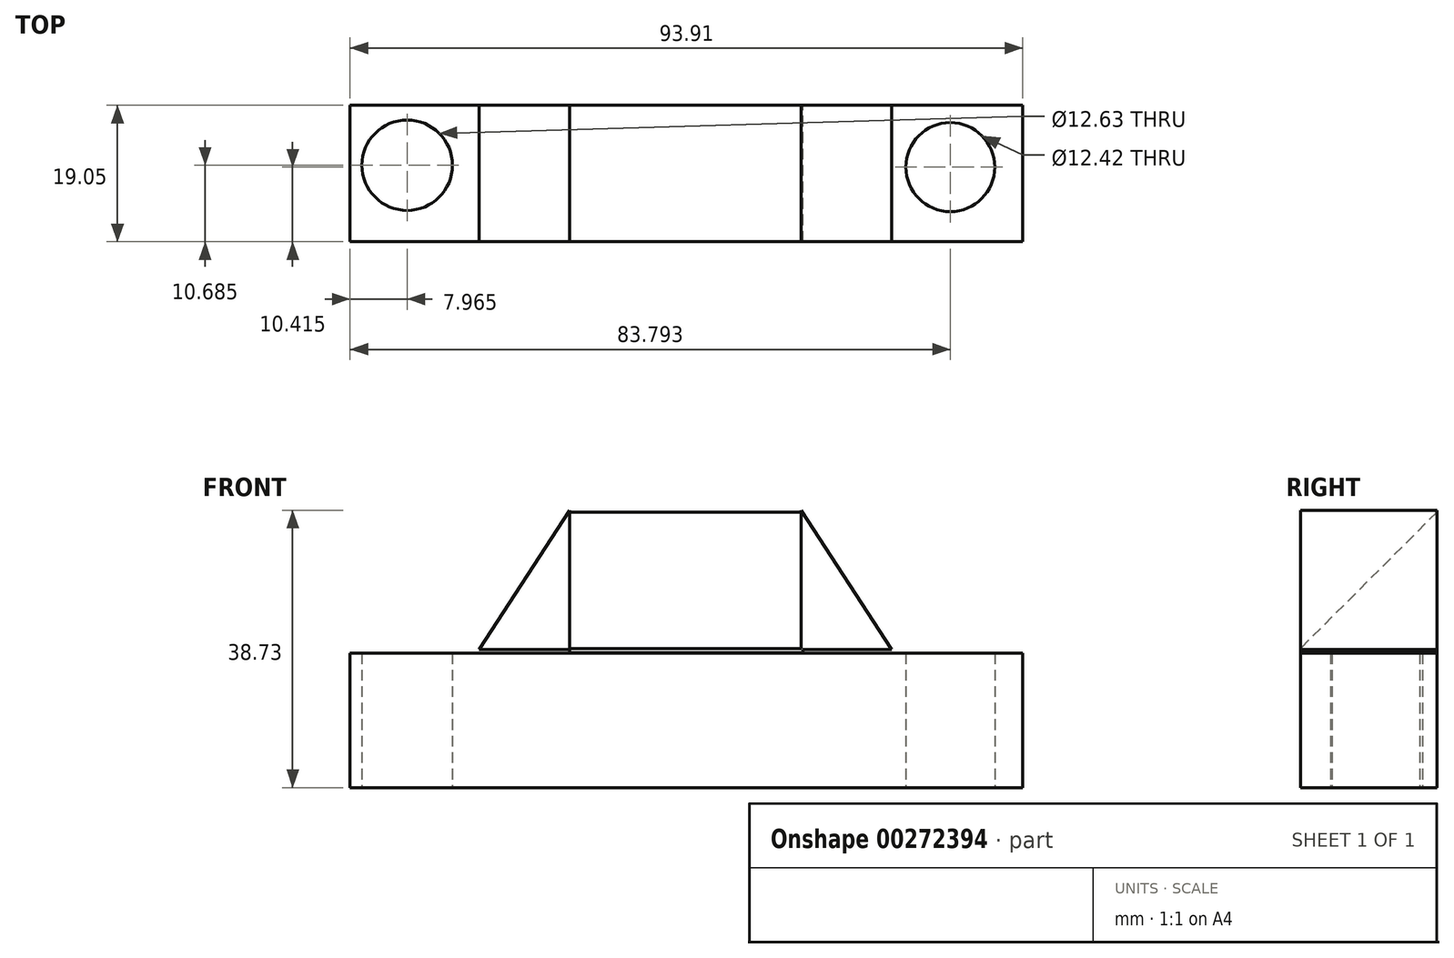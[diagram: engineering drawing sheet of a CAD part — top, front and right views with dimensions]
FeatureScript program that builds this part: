
annotation { "Feature Type Name" : "Feature", "Feature Type Description" : "" }
export const myFeature = defineFeature(function(context is Context, id is Id, definition is map)
    precondition{}
    {
        {
            var Q0;
            Q0=qCreatedBy(makeId("Front.planeOp"),FACE);
            var sketch = newSketch(context, id + "F0", { "sketchPlane" : qUnion([Q0])});
            skLineSegment(sketch, "E0.bottom", {"start": v(-44.26, 0) * mm, "end": v(49.65, 0) * mm});
            skLineSegment(sketch, "E0.top", {"start": v(-44.26, 18.75) * mm, "end": v(49.65, 18.75) * mm});
            skLineSegment(sketch, "E0.left", {"start": v(-44.26, 0) * mm, "end": v(-44.26, 18.75) * mm});
            skLineSegment(sketch, "E0.right", {"start": v(49.65, 0) * mm, "end": v(49.65, 18.75) * mm});
            skSolve(sketch);
        }
        {
            var Q0;
            Q0 = qSketchRegion(id + "F0", true);
            extrude(context, id + "F1", {"entities" : qUnion([Q0]), "depth" : 19.05 * mm});
        }
        {
            var Q0;
            Q0=qCreatedBy(makeId("Top.planeOp"),FACE);
            var sketch = newSketch(context, id + "F2", { "sketchPlane" : qUnion([Q0])});
            skCircle(sketch, "E1", {"center": v(39.53, -8.64) * mm, "radius": 6.21 * mm});
            skCircle(sketch, "E2", {"center": v(-36.3, -8.37) * mm, "radius": 6.32 * mm});
            skSolve(sketch);
        }
        {
            var Q0;
            Q0 = qSketchRegion(id + "F2", true);
            extrude(context, id + "F3", {"entities" : qUnion([Q0]), "operationType" : NewBodyOperationType.REMOVE, "depth" : 25.4 * mm});
        }
        {
            var Q0;
            Q0=qCreatedBy(makeId("Front.planeOp"),FACE);
            var sketch = newSketch(context, id + "F4", { "sketchPlane" : qUnion([Q0])});
            skLineSegment(sketch, "E3.bottom", {"start": v(-13.6, 18.82) * mm, "end": v(18.94, 18.82) * mm});
            skLineSegment(sketch, "E3.top", {"start": v(-13.6, 38.49) * mm, "end": v(18.94, 38.49) * mm});
            skLineSegment(sketch, "E3.left", {"start": v(-13.6, 18.82) * mm, "end": v(-13.6, 38.49) * mm});
            skLineSegment(sketch, "E3.right", {"start": v(18.94, 18.82) * mm, "end": v(18.94, 38.49) * mm});
            skSolve(sketch);
        }
        {
            var Q0;
            Q0 = qSketchRegion(id + "F4", true);
            extrude(context, id + "F5", {"entities" : qUnion([Q0]), "depth" : 19.05 * mm});
        }
        {
            var Q0;
            Q0=makeQuery(id+"F5.opExtrude","CAP_EDGE",EDGE,{"disambiguationData":[OSD([sQuery(id+"F4.wireOp",EDGE,"E3.top")])],"isStart":false});
            chamfer(context, id + "F6", {"entities" : qUnion([Q0]), "width" : 19.05 * mm, "tangentPropagation" : true});
        }
        {
            var Q0;
            Q0=qCreatedBy(makeId("Front.planeOp"),FACE);
            var sketch = newSketch(context, id + "F7", { "sketchPlane" : qUnion([Q0])});
            skLineSegment(sketch, "E4", {"start": v(18.7, 38.73) * mm, "end": v(18.7, 19.3) * mm});
            skLineSegment(sketch, "E5", {"start": v(18.7, 19.3) * mm, "end": v(31.32, 19.3) * mm});
            skLineSegment(sketch, "E6", {"start": v(31.32, 19.3) * mm, "end": v(18.7, 38.73) * mm});
            skLineSegment(sketch, "E7", {"start": v(-13.6, 38.73) * mm, "end": v(-13.6, 19.3) * mm});
            skLineSegment(sketch, "E8", {"start": v(-13.6, 19.3) * mm, "end": v(-26.22, 19.3) * mm});
            skLineSegment(sketch, "E9", {"start": v(-26.22, 19.3) * mm, "end": v(-13.6, 38.73) * mm});
            skSolve(sketch);
        }
        {
            var Q0;
            Q0 = qSketchRegion(id + "F7", true);
            extrude(context, id + "F8", {"entities" : qUnion([Q0]), "operationType" : NewBodyOperationType.ADD, "depth" : 19.05 * mm});
        }
    });
